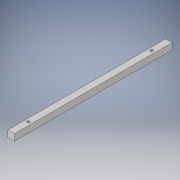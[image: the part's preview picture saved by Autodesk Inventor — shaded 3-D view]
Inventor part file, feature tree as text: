
AUTODESK INVENTOR PART (.ipt)
format: ipt  version: 2019 (Build 230136000, 136)  size: 109,056 bytes
history: native  units: mm
features: extrude x2, sketch x2
ambient origin geometry x8: Origin, YZ Plane, XZ Plane, XY Plane, X Axis, Y Axis, Z Axis, Center Point
bodies: Solid1 (feature_tree)
feature tree (4):
  extrude  "Extrusion1"  Depth=460.0mm
  extrude  "Extrusion2"  Depth=213.727452mm
  sketch  "Sketch1"  dims[d0=19.0mm d1=460.0mm]
  sketch  "Sketch2"  dims[d2=19.0mm d3=213.727452mm d4=19.0mm d5=0.0mm d6=50.0mm d7=50.0mm d8=9.5mm d9=9.5mm d10=8.0mm d11=8.0mm d12=19.0mm d13=0.0mm]
